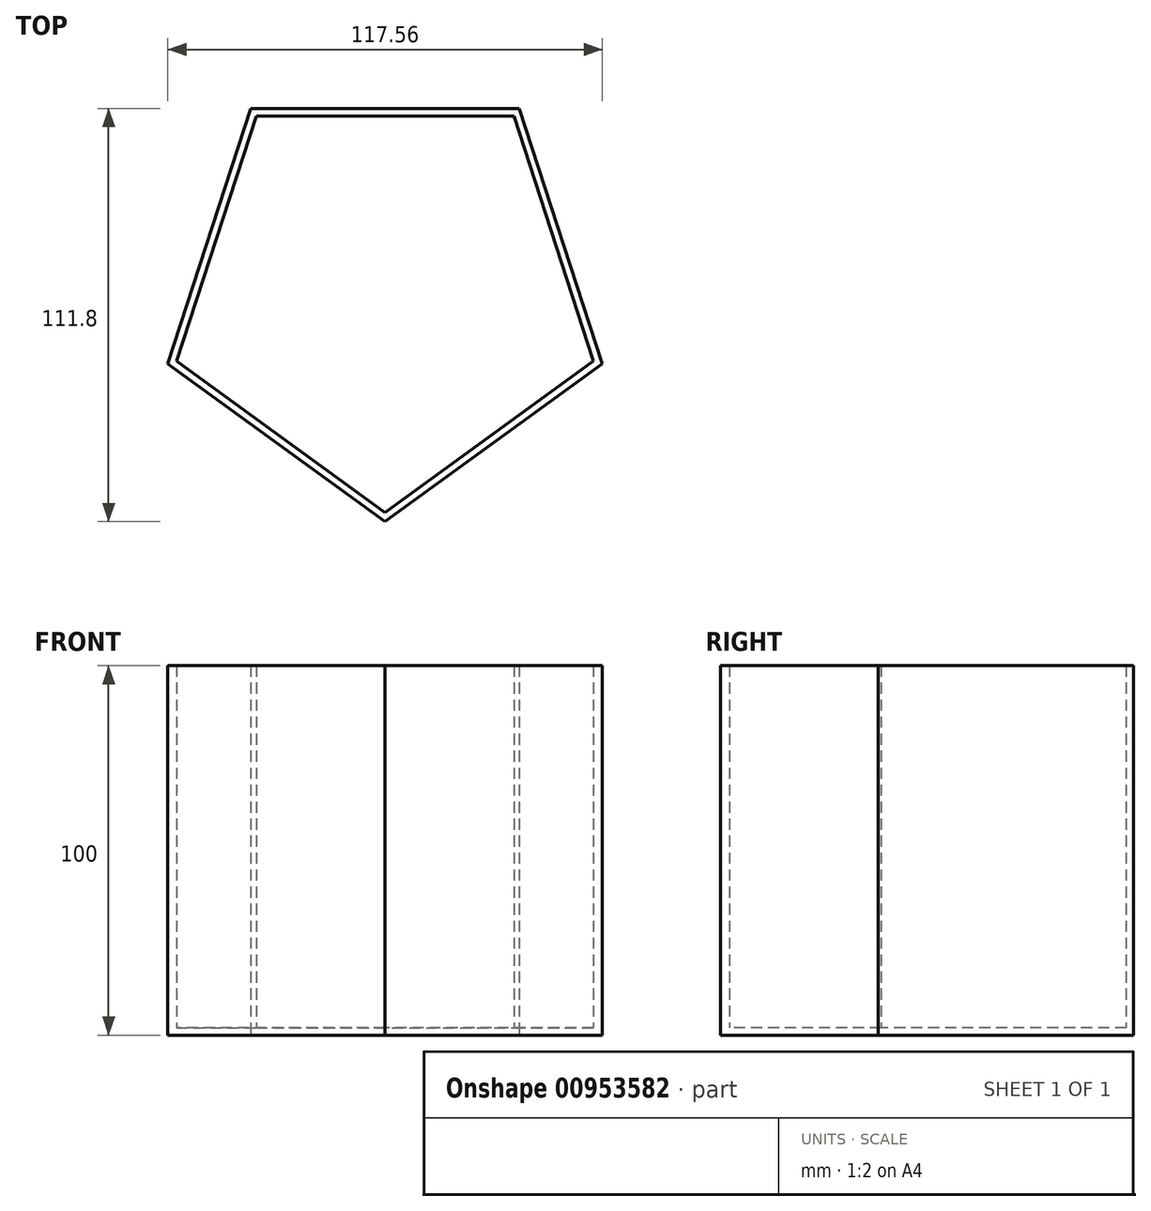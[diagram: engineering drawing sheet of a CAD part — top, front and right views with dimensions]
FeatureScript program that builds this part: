
annotation { "Feature Type Name" : "Feature", "Feature Type Description" : "" }
export const myFeature = defineFeature(function(context is Context, id is Id, definition is map)
    precondition{}
    {
        {
            var Q0;
            Q0=qCreatedBy(makeId("Top.planeOp"),FACE);
            var sketch = newSketch(context, id + "F0", { "sketchPlane" : qUnion([Q0])});
            skCircle(sketch, "E0.cCircle", {"center": v(0, 0) * mm, "radius": 50 * mm, "construction": true});
            skLineSegment(sketch, "E0.0", {"start": v(-36.33, 50) * mm, "end": v(36.33, 50) * mm});
            skLineSegment(sketch, "E0.1", {"start": v(36.33, 50) * mm, "end": v(58.78, -19.1) * mm});
            skLineSegment(sketch, "E0.2", {"start": v(58.78, -19.1) * mm, "end": v(0, -61.8) * mm});
            skLineSegment(sketch, "E0.3", {"start": v(0, -61.8) * mm, "end": v(-58.78, -19.1) * mm});
            skLineSegment(sketch, "E0.4", {"start": v(-58.78, -19.1) * mm, "end": v(-36.33, 50) * mm});
            skPoint(sketch, "E0.0.midPoint", {"position": v(0, 50) * mm});
            skLineSegment(sketch, "E1.0", {"start": v(34.87, 48) * mm, "end": v(56.43, -18.33) * mm});
            skLineSegment(sketch, "E1.1", {"start": v(-34.87, 48) * mm, "end": v(34.87, 48) * mm});
            skLineSegment(sketch, "E1.2", {"start": v(56.43, -18.33) * mm, "end": v(0, -59.33) * mm});
            skLineSegment(sketch, "E1.3", {"start": v(0, -59.33) * mm, "end": v(-56.43, -18.33) * mm});
            skLineSegment(sketch, "E1.4", {"start": v(-56.43, -18.33) * mm, "end": v(-34.87, 48) * mm});
            skSolve(sketch);
        }
        {
            var Q0;
            Q0=makeQuery(id+"F0.imprint","IMPRINT",FACE,{"disambiguationData":[TD([[makeQuery(id+"F0.imprint","IMPRINT",EDGE,{"derivedFrom":sQuery(id+"F0.wireOp",EDGE,"E0.0")}),-1.0]])]});
            extrude(context, id + "F1", {"entities" : qUnion([Q0]), "depth" : 100 * mm, "offsetDistance" : 25 * mm});
        }
        {
            var Q0;
            Q0=makeQuery(id+"F0.imprint","IMPRINT",FACE,{"disambiguationData":[TD([[makeQuery(id+"F0.imprint","IMPRINT",EDGE,{"derivedFrom":sQuery(id+"F0.wireOp",EDGE,"E1.0")}),-1.0]])]});
            extrude(context, id + "F2", {"entities" : qUnion([Q0]), "operationType" : NewBodyOperationType.ADD, "depth" : 2 * mm, "offsetDistance" : 25 * mm});
        }
    });
